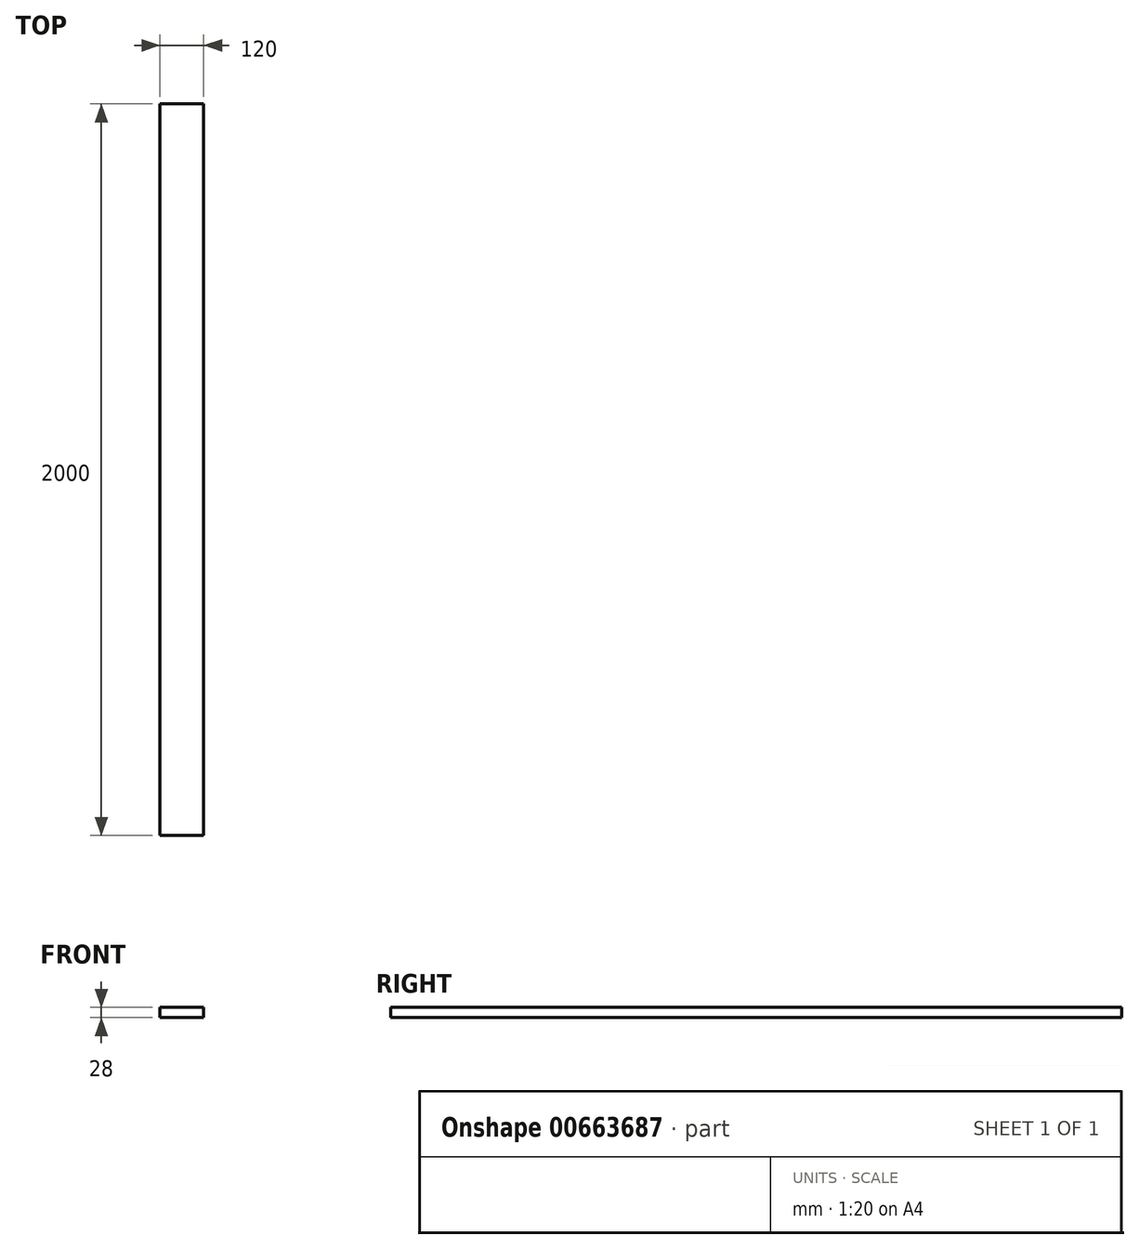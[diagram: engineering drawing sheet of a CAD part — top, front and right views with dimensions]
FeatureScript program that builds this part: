
annotation { "Feature Type Name" : "Feature", "Feature Type Description" : "" }
export const myFeature = defineFeature(function(context is Context, id is Id, definition is map)
    precondition{}
    {
        {
            var Q0;
            Q0=qCreatedBy(makeId("Front.planeOp"),FACE);
            var sketch = newSketch(context, id + "F0", { "sketchPlane" : qUnion([Q0])});
            skLineSegment(sketch, "E0.bottom", {"start": v(120, 0) * mm, "end": v(0, 0) * mm});
            skLineSegment(sketch, "E0.top", {"start": v(120, 28) * mm, "end": v(0, 28) * mm});
            skLineSegment(sketch, "E0.left", {"start": v(120, 0) * mm, "end": v(120, 28) * mm});
            skLineSegment(sketch, "E0.right", {"start": v(0, 0) * mm, "end": v(0, 28) * mm});
            skSolve(sketch);
        }
        {
            var Q0;
            Q0 = qSketchRegion(id + "F0", true);
            extrude(context, id + "F1", {"entities" : qUnion([Q0]), "depth" : 2000 * mm, "offsetDistance" : 25 * mm});
        }
    });
